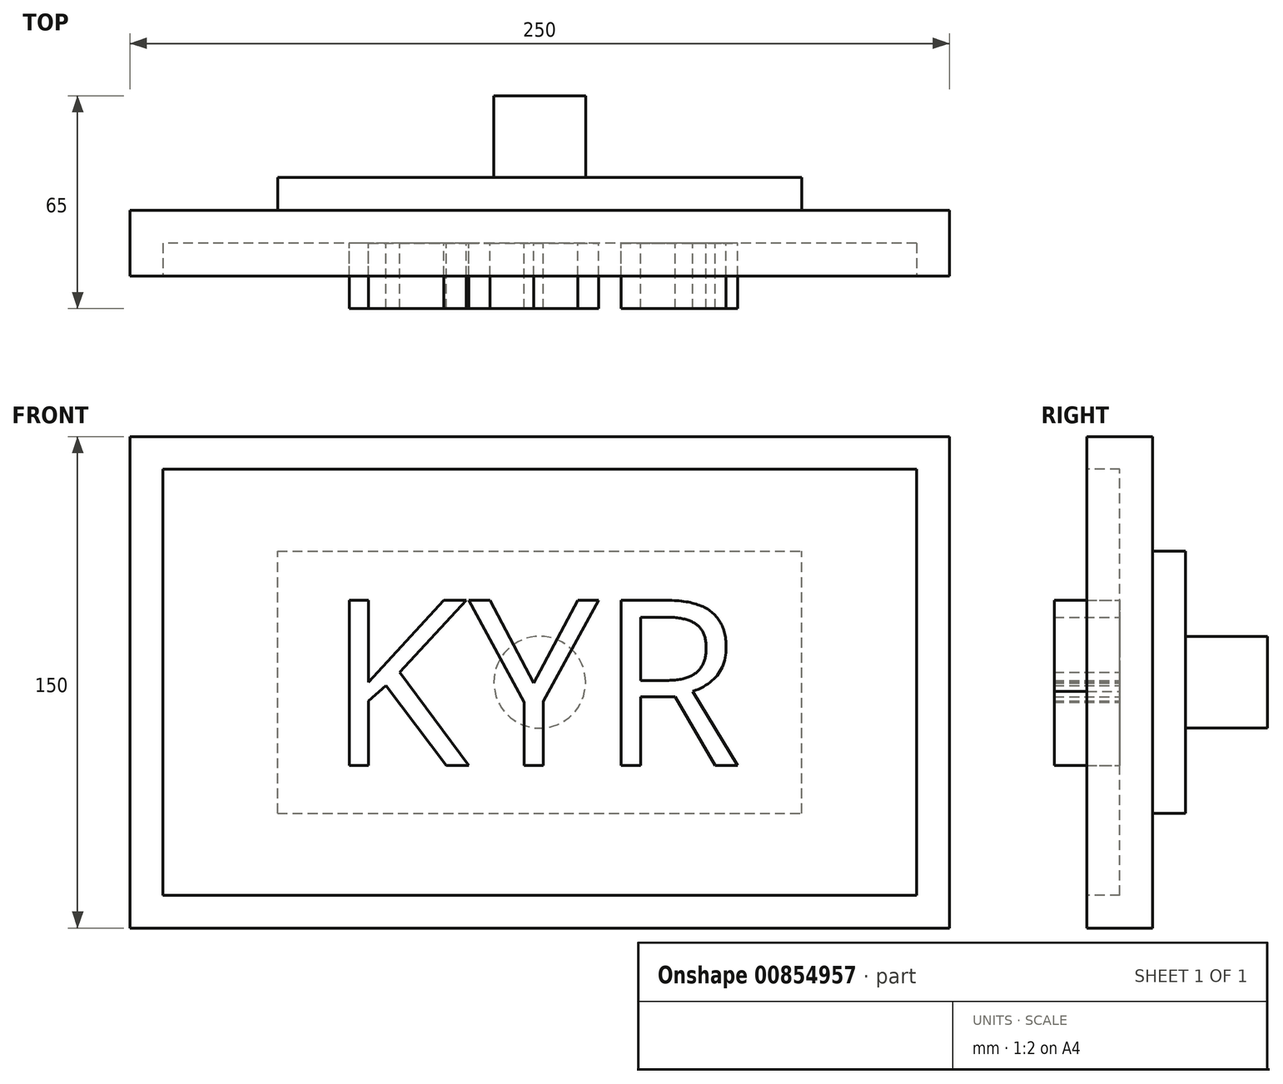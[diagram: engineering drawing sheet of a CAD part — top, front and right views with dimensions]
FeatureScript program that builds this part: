
annotation { "Feature Type Name" : "Feature", "Feature Type Description" : "" }
export const myFeature = defineFeature(function(context is Context, id is Id, definition is map)
    precondition{}
    {
        {
            var Q0;
            Q0=qCreatedBy(makeId("Front.planeOp"),FACE);
            var sketch = newSketch(context, id + "F0", { "sketchPlane" : qUnion([Q0])});
            skLineSegment(sketch, "E0.bottom", {"start": v(125, -75) * mm, "end": v(-125, -75) * mm});
            skLineSegment(sketch, "E0.top", {"start": v(125, 75) * mm, "end": v(-125, 75) * mm});
            skLineSegment(sketch, "E0.left", {"start": v(125, -75) * mm, "end": v(125, 75) * mm});
            skLineSegment(sketch, "E0.right", {"start": v(-125, -75) * mm, "end": v(-125, 75) * mm});
            skPoint(sketch, "E0.middle", {"position": v(0, 0) * mm});
            skSolve(sketch);
        }
        {
            var Q0;
            Q0=makeQuery(id+"F0.imprint","IMPRINT",FACE,{"disambiguationData":[TD([[makeQuery(id+"F0.imprint","IMPRINT",EDGE,{"derivedFrom":sQuery(id+"F0.wireOp",EDGE,"E0.bottom")}),-1.0]])]});
            extrude(context, id + "F1", {"entities" : qUnion([Q0]), "depth" : 20 * mm, "offsetDistance" : 25 * mm});
        }
        {
            var Q0;
            Q0=makeQuery(id+"F1.opExtrude","CAP_FACE",FACE,{"disambiguationData":[OSD([sQuery(id+"F0.wireOp",EDGE,"E0.bottom"),sQuery(id+"F0.wireOp",EDGE,"E0.top"),sQuery(id+"F0.wireOp",EDGE,"E0.left"),sQuery(id+"F0.wireOp",EDGE,"E0.right")])],"isStart":false});
            var sketch = newSketch(context, id + "F2", { "sketchPlane" : qUnion([Q0])});
            skLineSegment(sketch, "E1.bottom", {"start": v(115, -65) * mm, "end": v(-115, -65) * mm});
            skLineSegment(sketch, "E1.top", {"start": v(115, 65) * mm, "end": v(-115, 65) * mm});
            skLineSegment(sketch, "E1.left", {"start": v(115, -65) * mm, "end": v(115, 65) * mm});
            skLineSegment(sketch, "E1.right", {"start": v(-115, -65) * mm, "end": v(-115, 65) * mm});
            skPoint(sketch, "E1.middle", {"position": v(0, 0) * mm});
            skSolve(sketch);
        }
        {
            var Q0;
            Q0 = qSketchRegion(id + "F2", true);
            extrude(context, id + "F3", {"entities" : qUnion([Q0]), "operationType" : NewBodyOperationType.REMOVE, "oppositeDirection" : true, "depth" : 10 * mm, "offsetDistance" : 25 * mm});
        }
        {
            var Q0;
            Q0=makeQuery(id+"F1.opExtrude","CAP_FACE",FACE,{"disambiguationData":[OSD([sQuery(id+"F0.wireOp",EDGE,"E0.bottom"),sQuery(id+"F0.wireOp",EDGE,"E0.top"),sQuery(id+"F0.wireOp",EDGE,"E0.left"),sQuery(id+"F0.wireOp",EDGE,"E0.right")])],"isStart":true});
            var sketch = newSketch(context, id + "F4", { "sketchPlane" : qUnion([Q0])});
            skLineSegment(sketch, "E2.bottom", {"start": v(80, -40) * mm, "end": v(-80, -40) * mm});
            skLineSegment(sketch, "E2.top", {"start": v(80, 40) * mm, "end": v(-80, 40) * mm});
            skLineSegment(sketch, "E2.left", {"start": v(80, -40) * mm, "end": v(80, 40) * mm});
            skLineSegment(sketch, "E2.right", {"start": v(-80, -40) * mm, "end": v(-80, 40) * mm});
            skPoint(sketch, "E2.middle", {"position": v(0, 0) * mm});
            skSolve(sketch);
        }
        {
            var Q0;
            Q0=makeQuery(id+"F4.imprint","IMPRINT",FACE,{"disambiguationData":[TD([[makeQuery(id+"F4.imprint","IMPRINT",EDGE,{"derivedFrom":sQuery(id+"F4.wireOp",EDGE,"E2.bottom")}),-1.0]])]});
            extrude(context, id + "F5", {"entities" : qUnion([Q0]), "operationType" : NewBodyOperationType.ADD, "depth" : 10 * mm, "offsetDistance" : 25 * mm});
        }
        {
            var Q0;
            Q0=makeQuery(id+"F5.opExtrude","CAP_FACE",FACE,{"disambiguationData":[OSD([sQuery(id+"F4.wireOp",EDGE,"E2.bottom"),sQuery(id+"F4.wireOp",EDGE,"E2.top"),sQuery(id+"F4.wireOp",EDGE,"E2.left"),sQuery(id+"F4.wireOp",EDGE,"E2.right")])],"isStart":false});
            var sketch = newSketch(context, id + "F6", { "sketchPlane" : qUnion([Q0])});
            skCircle(sketch, "E3", {"center": v(0, 0) * mm, "radius": 14 * mm});
            skSolve(sketch);
        }
        {
            var Q0;
            Q0 = qSketchRegion(id + "F6", true);
            extrude(context, id + "F7", {"entities" : qUnion([Q0]), "operationType" : NewBodyOperationType.ADD, "depth" : 25 * mm, "offsetDistance" : 25 * mm});
        }
        {
            var Q0;
            Q0=makeQuery(id+"F3.boolean.opBoolean","COPY",FACE,{"derivedFrom":makeQuery(id+"F3.opExtrude","CAP_FACE",FACE,{"disambiguationData":[OSD([sQuery(id+"F2.wireOp",EDGE,"E1.bottom"),sQuery(id+"F2.wireOp",EDGE,"E1.top"),sQuery(id+"F2.wireOp",EDGE,"E1.left"),sQuery(id+"F2.wireOp",EDGE,"E1.right")])],"isStart":false})});
            var sketch = newSketch(context, id + "F8", { "sketchPlane" : qUnion([Q0])});
            skText(sketch, "E4", { "text": "KYR", "fontName": "OpenSans-Regular.ttf"});
            const initialGuessF8  = {"E4": [-0.065, -0.02544, 1, 0, 0.05088]};
            skSetInitialGuess(sketch, initialGuessF8);
            skSolve(sketch);
        }
        {
            var Q0;
            Q0 = qSketchRegion(id + "F8", true);
            extrude(context, id + "F9", {"entities" : qUnion([Q0]), "operationType" : NewBodyOperationType.ADD, "depth" : 20 * mm, "offsetDistance" : 25 * mm});
        }
    });
